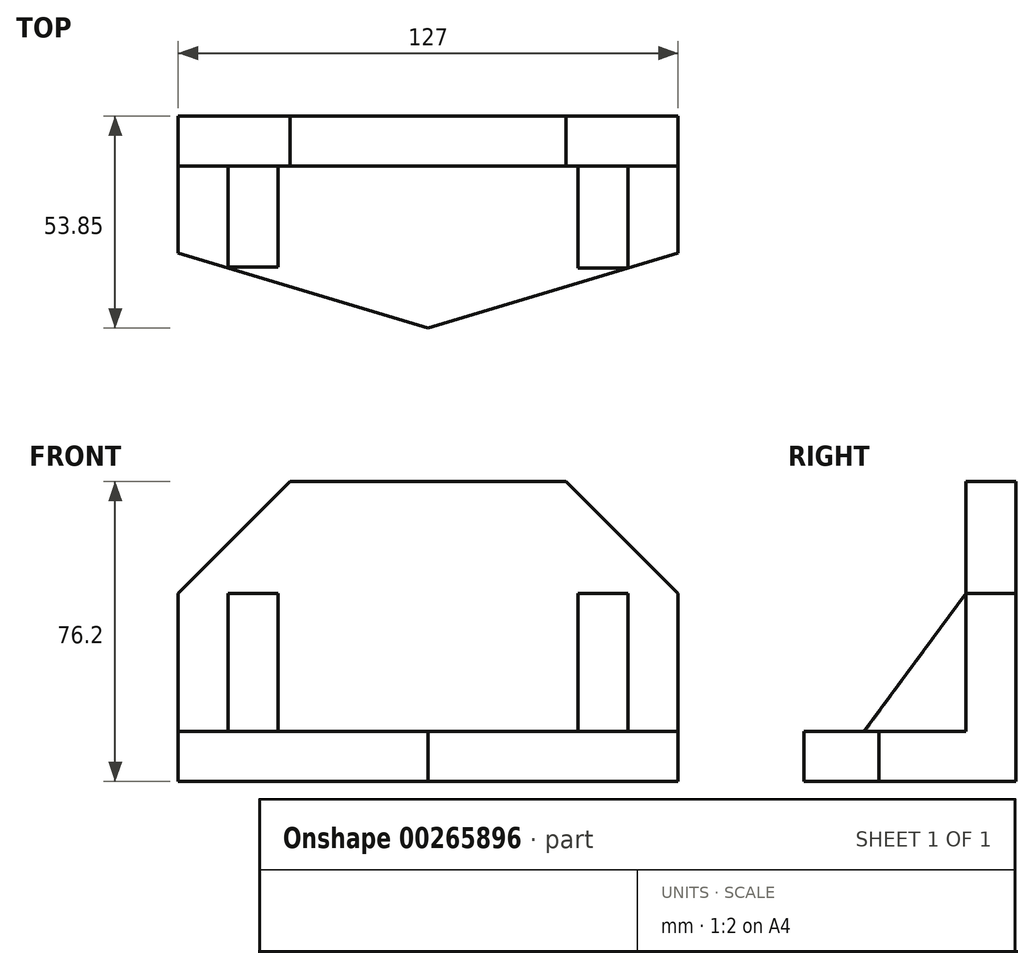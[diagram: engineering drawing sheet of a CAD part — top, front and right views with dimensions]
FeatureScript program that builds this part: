
annotation { "Feature Type Name" : "Feature", "Feature Type Description" : "" }
export const myFeature = defineFeature(function(context is Context, id is Id, definition is map)
    precondition{}
    {
        {
            var Q0;
            Q0=qCreatedBy(makeId("Front.planeOp"),FACE);
            var sketch = newSketch(context, id + "F0", { "sketchPlane" : qUnion([Q0])});
            skLineSegment(sketch, "E0.bottom", {"start": v(-65.36, 25.26) * mm, "end": v(61.64, 25.26) * mm});
            skLineSegment(sketch, "E0.top", {"start": v(-65.36, -50.94) * mm, "end": v(61.64, -50.94) * mm});
            skLineSegment(sketch, "E0.left", {"start": v(-65.36, 25.26) * mm, "end": v(-65.36, -50.94) * mm});
            skLineSegment(sketch, "E0.right", {"start": v(61.64, 25.26) * mm, "end": v(61.64, -50.94) * mm});
            skSolve(sketch);
        }
        {
            var Q0;
            Q0 = qSketchRegion(id + "F0", true);
            extrude(context, id + "F1", {"entities" : qUnion([Q0]), "depth" : 53.85 * mm});
        }
        {
            var Q0;
            Q0=makeQuery(id+"F1.opExtrude","SWEPT_FACE",FACE,{"disambiguationData":[OSD([sQuery(id+"F0.wireOp",EDGE,"E0.bottom")])]});
            var sketch = newSketch(context, id + "F2", { "sketchPlane" : qUnion([Q0])});
            skLineSegment(sketch, "E1.bottom", {"start": v(-65.36, -12.7) * mm, "end": v(61.64, -12.7) * mm});
            skLineSegment(sketch, "E1.top", {"start": v(-65.36, -53.85) * mm, "end": v(61.64, -53.85) * mm});
            skLineSegment(sketch, "E1.left", {"start": v(-65.36, -12.7) * mm, "end": v(-65.36, -53.85) * mm});
            skLineSegment(sketch, "E1.right", {"start": v(61.64, -12.7) * mm, "end": v(61.64, -53.85) * mm});
            skSolve(sketch);
        }
        {
            var Q0;
            Q0=makeQuery(id+"F2.imprint","IMPRINT",FACE,{"disambiguationData":[TD([[makeQuery(id+"F2.imprint","IMPRINT",EDGE,{"derivedFrom":sQuery(id+"F2.wireOp",EDGE,"E1.bottom")}),-1.0]])]});
            extrude(context, id + "F3", {"entities" : qUnion([Q0]), "operationType" : NewBodyOperationType.REMOVE, "oppositeDirection" : true, "depth" : 63.5 * mm});
        }
        {
            var Q0;
            Q0=makeQuery(id+"F3.boolean.opBoolean","COPY",FACE,{"derivedFrom":makeQuery(id+"F3.opExtrude","SWEPT_FACE",FACE,{"disambiguationData":[OSD([sQuery(id+"F2.wireOp",EDGE,"E1.bottom")])]})});
            var sketch = newSketch(context, id + "F4", { "sketchPlane" : qUnion([Q0])});
            skLineSegment(sketch, "E2", {"start": v(-65.36, 25.26) * mm, "end": v(-65.36, -3.18) * mm});
            skLineSegment(sketch, "E3", {"start": v(-65.36, 25.26) * mm, "end": v(-36.92, 25.26) * mm});
            skLineSegment(sketch, "E4", {"start": v(61.64, 25.26) * mm, "end": v(33.19, 25.26) * mm});
            skLineSegment(sketch, "E5", {"start": v(61.64, 25.26) * mm, "end": v(61.64, -3.18) * mm});
            skLineSegment(sketch, "E6", {"start": v(-36.92, 25.26) * mm, "end": v(-65.36, -3.18) * mm});
            skLineSegment(sketch, "E7", {"start": v(33.19, 25.26) * mm, "end": v(61.64, -3.18) * mm});
            skSolve(sketch);
        }
        {
            var Q0;
            Q0=makeQuery(id+"F4.imprint","IMPRINT",FACE,{"disambiguationData":[TD([[makeQuery(id+"F4.imprint","IMPRINT",EDGE,{"derivedFrom":sQuery(id+"F4.wireOp",EDGE,"E2")}),-1.0]])]});
            var Q1;
            Q1=makeQuery(id+"F4.imprint","IMPRINT",FACE,{"disambiguationData":[TD([[makeQuery(id+"F4.imprint","IMPRINT",EDGE,{"derivedFrom":sQuery(id+"F4.wireOp",EDGE,"E4")}),-1.0]])]});
            extrude(context, id + "F5", {"entities" : qUnion([Q0, Q1]), "operationType" : NewBodyOperationType.REMOVE, "oppositeDirection" : true, "depth" : 12.7 * mm});
        }
        {
            var Q0;
            Q0=makeQuery(id+"F3.boolean.opBoolean","COPY",FACE,{"derivedFrom":makeQuery(id+"F3.opExtrude","CAP_FACE",FACE,{"disambiguationData":[OSD([sQuery(id+"F2.wireOp",EDGE,"E1.bottom"),sQuery(id+"F2.wireOp",EDGE,"E1.top"),sQuery(id+"F2.wireOp",EDGE,"E1.left"),sQuery(id+"F2.wireOp",EDGE,"E1.right")])],"isStart":false})});
            var sketch = newSketch(context, id + "F6", { "sketchPlane" : qUnion([Q0])});
            skLineSegment(sketch, "E8", {"start": v(61.64, -53.85) * mm, "end": v(61.64, -34.8) * mm});
            skLineSegment(sketch, "E9", {"start": v(-65.36, -53.85) * mm, "end": v(-65.36, -34.8) * mm});
            skLineSegment(sketch, "E10", {"start": v(61.64, -53.85) * mm, "end": v(-1.86, -53.85) * mm});
            skLineSegment(sketch, "E11", {"start": v(-65.36, -34.8) * mm, "end": v(-1.86, -53.85) * mm});
            skLineSegment(sketch, "E12", {"start": v(61.64, -34.8) * mm, "end": v(-1.86, -53.85) * mm});
            skSolve(sketch);
        }
        {
            var Q0;
            {var subQ0=sQuery(id+"F6.wireOp",EDGE,"E9");Q0=makeQuery(id+"F6.imprint","IMPRINT",FACE,{"disambiguationData":[TD([[makeQuery(id+"F6.imprint","IMPRINT",EDGE,{"derivedFrom":subQ0}),-1.0]])]});}
            var Q1;
            Q1=makeQuery(id+"F6.imprint","IMPRINT",FACE,{"disambiguationData":[TD([[makeQuery(id+"F6.imprint","IMPRINT",EDGE,{"derivedFrom":sQuery(id+"F6.wireOp",EDGE,"E8")}),1.0]])]});
            extrude(context, id + "F7", {"entities" : qUnion([Q0, Q1]), "operationType" : NewBodyOperationType.REMOVE, "oppositeDirection" : true, "depth" : 12.7 * mm});
        }
        {
            var Q0;
            Q0=makeQuery(id+"F3.boolean.opBoolean","COPY",FACE,{"derivedFrom":makeQuery(id+"F3.opExtrude","CAP_FACE",FACE,{"disambiguationData":[OSD([sQuery(id+"F2.wireOp",EDGE,"E1.bottom"),sQuery(id+"F2.wireOp",EDGE,"E1.top"),sQuery(id+"F2.wireOp",EDGE,"E1.left"),sQuery(id+"F2.wireOp",EDGE,"E1.right")])],"isStart":false})});
            var sketch = newSketch(context, id + "F8", { "sketchPlane" : qUnion([Q0])});
            skLineSegment(sketch, "E13", {"start": v(61.64, -12.7) * mm, "end": v(48.94, -12.7) * mm});
            skLineSegment(sketch, "E14.bottom", {"start": v(48.94, -12.7) * mm, "end": v(36.24, -12.7) * mm});
            skLineSegment(sketch, "E14.top", {"start": v(48.94, -38.84) * mm, "end": v(36.24, -38.84) * mm});
            skLineSegment(sketch, "E14.left", {"start": v(48.94, -12.7) * mm, "end": v(48.94, -38.84) * mm});
            skLineSegment(sketch, "E14.right", {"start": v(36.24, -12.7) * mm, "end": v(36.24, -38.84) * mm});
            skSolve(sketch);
        }
        {
            var Q0;
            Q0 = qSketchRegion(id + "F8", true);
            extrude(context, id + "F9", {"entities" : qUnion([Q0]), "operationType" : NewBodyOperationType.ADD, "depth" : 35.05 * mm});
        }
        {
            var Q0;
            Q0=makeQuery(id+"F9.opExtrude","SWEPT_FACE",FACE,{"disambiguationData":[OSD([sQuery(id+"F8.wireOp",EDGE,"E14.left")])]});
            var sketch = newSketch(context, id + "F10", { "sketchPlane" : qUnion([Q0])});
            skLineSegment(sketch, "E15", {"start": v(-38.6, -38.24) * mm, "end": v(-12.7, -3.18) * mm});
            skSolve(sketch);
        }
        {
            var Q0;
            Q0=makeQuery(id+"F10.imprint","IMPRINT",FACE,{"disambiguationData":[TD([[makeQuery(id+"F10.imprint","IMPRINT",EDGE,{"derivedFrom":sQuery(id+"F10.wireOp",EDGE,"E15")}),1.0]])]});
            extrude(context, id + "F11", {"entities" : qUnion([Q0]), "operationType" : NewBodyOperationType.REMOVE, "oppositeDirection" : true, "depth" : 12.7 * mm});
        }
        {
            var Q0;
            {var subQ0=sQuery(id+"F8.wireOp",EDGE,"E14.top");var subQ1=makeQuery(id+"F9.opExtrude","SWEPT_FACE",FACE,{"disambiguationData":[OSD([subQ0])]});var subQ3=sQuery(id+"F8.wireOp",EDGE,"E14.left");var subQ6=sQuery(id+"F2.wireOp",EDGE,"E1.bottom");var subQ7=makeQuery(id+"F3.boolean.opBoolean","COPY",FACE,{"derivedFrom":makeQuery(id+"F3.opExtrude","CAP_FACE",FACE,{"disambiguationData":[OSD([subQ6,sQuery(id+"F2.wireOp",EDGE,"E1.top"),sQuery(id+"F2.wireOp",EDGE,"E1.left"),sQuery(id+"F2.wireOp",EDGE,"E1.right")])],"isStart":false})});Q0=makeQuery(id+"F11.boolean.opBoolean","MERGE",FACE,{"derivedFrom":[makeQuery(id+"F9.boolean.opBoolean","SPLIT",FACE,{"disambiguationData":[TD([makeQuery(id+"F1.opExtrude","SWEPT_FACE",FACE,{"disambiguationData":[OSD([sQuery(id+"F0.wireOp",EDGE,"E0.left")])]})])],"derivedFrom":subQ7}),makeQuery(id+"F11.opExtrude","SWEPT_FACE",FACE,{"disambiguationData":[OSD([subQ3]),TDD([makeQuery(id+"F10.imprint","IMPRINT",EDGE,{"derivedFrom":makeQuery(id+"F9.boolean.opBoolean","SPLIT",EDGE,{"disambiguationData":[TD([subQ1])],"derivedFrom":makeQuery(id+"F9.opExtrude","CAP_EDGE",EDGE,{"disambiguationData":[OSD([subQ3])],"isStart":true})})})])]})]});}
            var sketch = newSketch(context, id + "F12", { "sketchPlane" : qUnion([Q0])});
            skLineSegment(sketch, "E16", {"start": v(-65.36, -12.7) * mm, "end": v(-52.66, -12.7) * mm});
            skLineSegment(sketch, "E17", {"start": v(-52.66, -12.7) * mm, "end": v(-39.96, -12.7) * mm});
            skLineSegment(sketch, "E18.top", {"start": v(-52.66, -38.38) * mm, "end": v(-39.96, -38.38) * mm});
            skLineSegment(sketch, "E18.left", {"start": v(-52.66, -12.7) * mm, "end": v(-52.66, -38.38) * mm});
            skLineSegment(sketch, "E18.right", {"start": v(-39.96, -12.7) * mm, "end": v(-39.96, -38.38) * mm});
            skSolve(sketch);
        }
        {
            var Q0;
            Q0=makeQuery(id+"F12.imprint","IMPRINT",FACE,{"disambiguationData":[TD([[makeQuery(id+"F12.imprint","IMPRINT",EDGE,{"derivedFrom":sQuery(id+"F12.wireOp",EDGE,"E17")}),-1.0]])]});
            extrude(context, id + "F13", {"entities" : qUnion([Q0]), "operationType" : NewBodyOperationType.ADD, "depth" : 35.05 * mm});
        }
        {
            var Q0;
            Q0=makeQuery(id+"F13.opExtrude","SWEPT_FACE",FACE,{"disambiguationData":[OSD([sQuery(id+"F12.wireOp",EDGE,"E18.left")])]});
            var sketch = newSketch(context, id + "F14", { "sketchPlane" : qUnion([Q0])});
            skLineSegment(sketch, "E19", {"start": v(12.7, -3.18) * mm, "end": v(38.38, -38.24) * mm});
            skSolve(sketch);
        }
        {
            var Q0;
            Q0=makeQuery(id+"F14.imprint","IMPRINT",FACE,{"disambiguationData":[TD([[makeQuery(id+"F14.imprint","IMPRINT",EDGE,{"derivedFrom":sQuery(id+"F14.wireOp",EDGE,"E19")}),1.0]])]});
            extrude(context, id + "F15", {"entities" : qUnion([Q0]), "operationType" : NewBodyOperationType.REMOVE, "oppositeDirection" : true, "depth" : 12.7 * mm});
        }
    });
